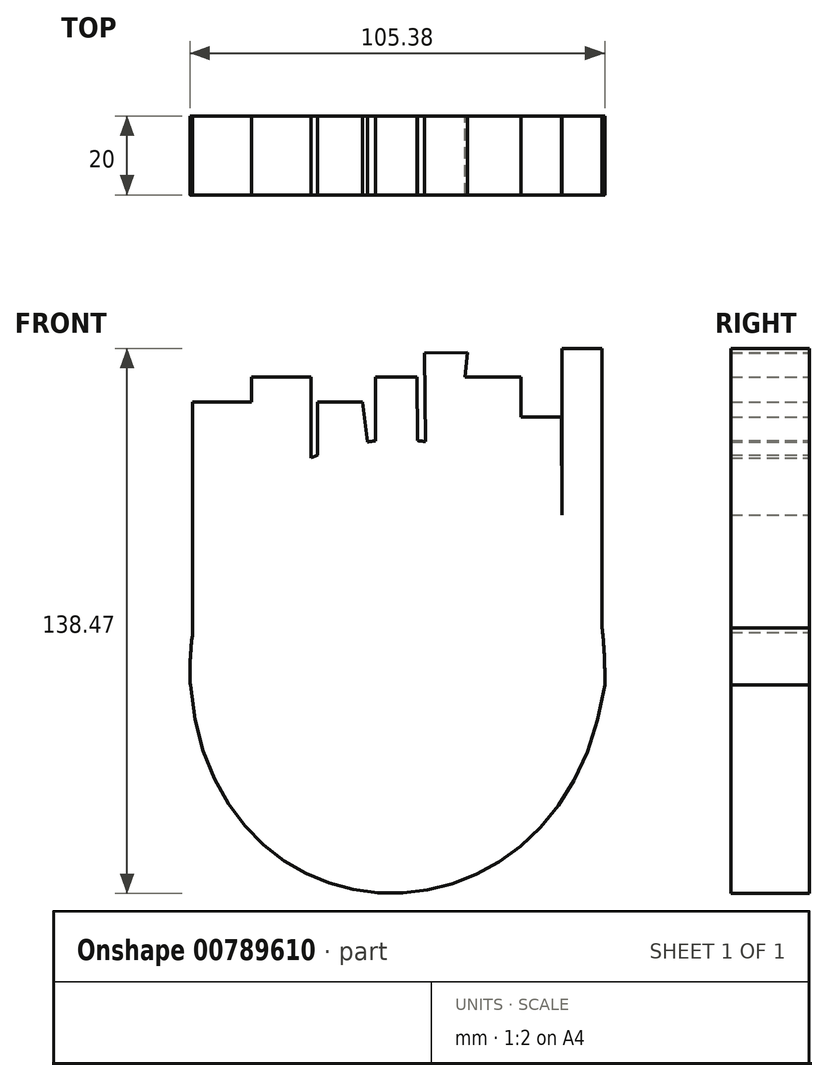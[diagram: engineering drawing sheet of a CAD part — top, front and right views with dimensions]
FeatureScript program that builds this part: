
annotation { "Feature Type Name" : "Feature", "Feature Type Description" : "" }
export const myFeature = defineFeature(function(context is Context, id is Id, definition is map)
    precondition{}
    {
        {
            var Q0;
            Q0=qCreatedBy(makeId("Front.planeOp"),FACE);
            var sketch = newSketch(context, id + "F0", { "sketchPlane" : qUnion([Q0])});
            skFitSpline(sketch, "E0", {"points": [v(0, 62.47) * mm, v(-52.37, 0) * mm], "startDerivative": vector(-139.6, -5.66) * mm, "endDerivative": vector(3.18, -52.9) * mm});
            skFitSpline(sketch, "E1", {"points": [v(0, 62.47) * mm, v(52.9, 0) * mm], "startDerivative": vector(126.08, -4.86) * mm, "endDerivative": vector(-1.5, -96.52) * mm});
            skFitSpline(sketch, "E2", {"points": [v(-52.37, 0) * mm, v(52.9, 0) * mm], "startDerivative": vector(17.12, -209.6) * mm, "endDerivative": vector(31.82, 213.58) * mm});
            skLineSegment(sketch, "E3", {"start": v(-51.76, 13.35) * mm, "end": v(-51.76, 71.93) * mm});
            skLineSegment(sketch, "E4", {"start": v(-51.76, 71.93) * mm, "end": v(-36.85, 71.93) * mm});
            skLineSegment(sketch, "E5", {"start": v(-36.85, 71.93) * mm, "end": v(-36.85, 47.02) * mm});
            skLineSegment(sketch, "E6", {"start": v(-36.85, 47.02) * mm, "end": v(-36.85, 78.35) * mm});
            skLineSegment(sketch, "E7", {"start": v(-36.85, 78.35) * mm, "end": v(-21.72, 78.35) * mm});
            skLineSegment(sketch, "E8", {"start": v(-21.72, 78.35) * mm, "end": v(-21.72, 47.02) * mm});
            skLineSegment(sketch, "E9", {"start": v(-21.72, 47.02) * mm, "end": v(-21.72, 71.93) * mm});
            skLineSegment(sketch, "E10", {"start": v(-5.4, 71.93) * mm, "end": v(-5.4, 47.02) * mm});
            skLineSegment(sketch, "E11", {"start": v(-5.4, 47.02) * mm, "end": v(-5.4, 78.35) * mm});
            skLineSegment(sketch, "E12", {"start": v(-5.4, 78.35) * mm, "end": v(5.2, 78.35) * mm});
            skLineSegment(sketch, "E13", {"start": v(4.1, 18.15) * mm, "end": v(8.4, 29.61) * mm});
            skLineSegment(sketch, "E14", {"start": v(7.13, 84.43) * mm, "end": v(18.09, 84.52) * mm});
            skLineSegment(sketch, "E15", {"start": v(18.09, 84.52) * mm, "end": v(13.52, 41.23) * mm});
            skLineSegment(sketch, "E16", {"start": v(13.52, 41.23) * mm, "end": v(17.44, 78.35) * mm});
            skLineSegment(sketch, "E17", {"start": v(17.44, 78.35) * mm, "end": v(31.56, 78.35) * mm});
            skLineSegment(sketch, "E18", {"start": v(31.56, 78.35) * mm, "end": v(31.56, 41.23) * mm});
            skLineSegment(sketch, "E19", {"start": v(31.56, 41.23) * mm, "end": v(31.56, 68.14) * mm});
            skLineSegment(sketch, "E20", {"start": v(31.56, 68.14) * mm, "end": v(41.93, 68.14) * mm});
            skLineSegment(sketch, "E21", {"start": v(41.93, 68.14) * mm, "end": v(42.03, 36.34) * mm});
            skLineSegment(sketch, "E22", {"start": v(42.03, 36.34) * mm, "end": v(42.03, 85.57) * mm});
            skLineSegment(sketch, "E23", {"start": v(52.21, 14.57) * mm, "end": v(52.21, 85.57) * mm});
            skLineSegment(sketch, "E24", {"start": v(52.21, 85.57) * mm, "end": v(42.03, 85.57) * mm});
            skLineSegment(sketch, "E25", {"start": v(7.13, 84.43) * mm, "end": v(7.52, 37.28) * mm});
            skLineSegment(sketch, "E26", {"start": v(5.2, 78.35) * mm, "end": v(5.53, 39.93) * mm});
            skLineSegment(sketch, "E27", {"start": v(5.53, 39.93) * mm, "end": v(5.23, 75.45) * mm});
            skLineSegment(sketch, "E28", {"start": v(-22.47, 38.39) * mm, "end": v(-21.72, 33.43) * mm});
            skLineSegment(sketch, "E29", {"start": v(-22.47, 38.39) * mm, "end": v(-31.9, 26.11) * mm});
            skLineSegment(sketch, "E30", {"start": v(-8.68, 71.93) * mm, "end": v(-5.4, 47.02) * mm});
            skLineSegment(sketch, "E31", {"start": v(-20.06, 71.93) * mm, "end": v(-20.06, 42.33) * mm});
            skLineSegment(sketch, "E32", {"start": v(-20.06, 71.93) * mm, "end": v(-8.68, 71.93) * mm});
            skSolve(sketch);
        }
        {
            var Q0;
            Q0 = qSketchRegion(id + "F0", true);
            extrude(context, id + "F1", {"entities" : qUnion([Q0]), "depth" : 20 * mm, "offsetDistance" : 25 * mm});
        }
    });
